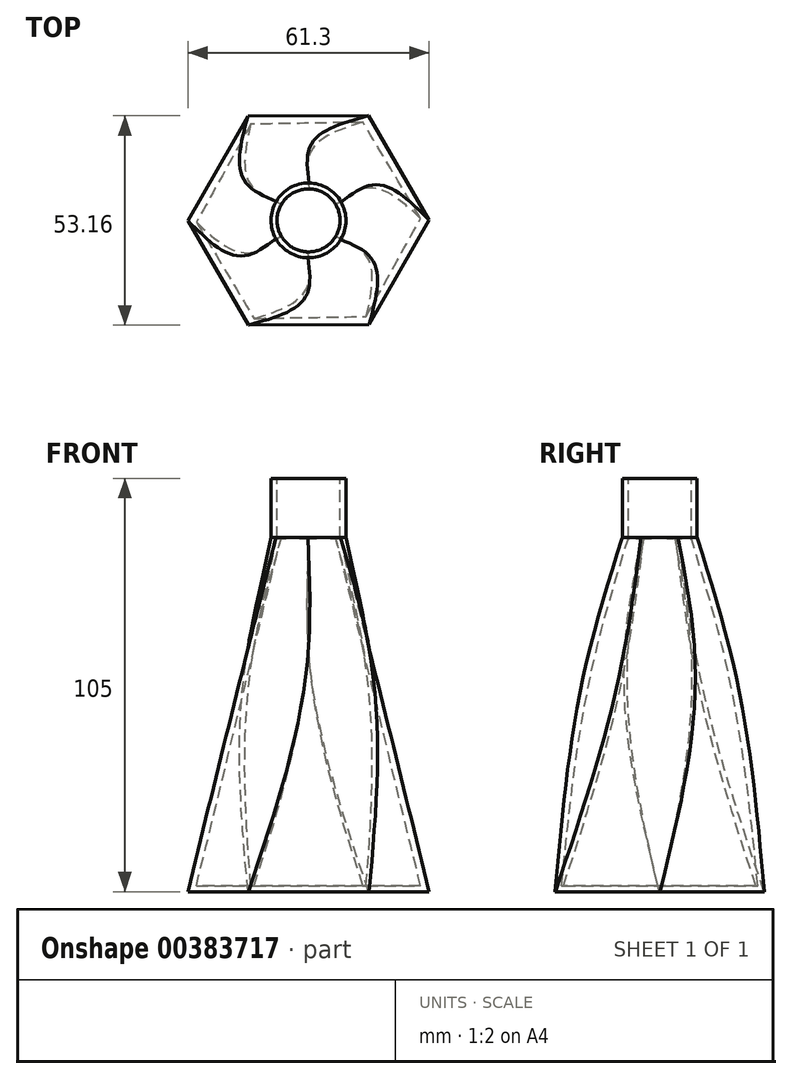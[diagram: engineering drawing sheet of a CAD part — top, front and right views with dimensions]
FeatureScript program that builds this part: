
annotation { "Feature Type Name" : "Feature", "Feature Type Description" : "" }
export const myFeature = defineFeature(function(context is Context, id is Id, definition is map)
    precondition{}
    {
        {
            var Q0;
            Q0=qCreatedBy(makeId("Top.planeOp"),FACE);
            var sketch = newSketch(context, id + "F0", { "sketchPlane" : qUnion([Q0])});
            skCircle(sketch, "E0.cCircle", {"center": v(0, 0) * mm, "radius": 26.54 * mm, "construction": true});
            skLineSegment(sketch, "E0.0", {"start": v(-30.65, -0.07) * mm, "end": v(-15.38, 26.5) * mm});
            skLineSegment(sketch, "E0.1", {"start": v(-15.38, 26.5) * mm, "end": v(15.26, 26.58) * mm});
            skLineSegment(sketch, "E0.2", {"start": v(15.26, 26.58) * mm, "end": v(30.65, 0.07) * mm});
            skLineSegment(sketch, "E0.3", {"start": v(30.65, 0.07) * mm, "end": v(15.38, -26.5) * mm});
            skLineSegment(sketch, "E0.4", {"start": v(15.38, -26.5) * mm, "end": v(-15.26, -26.58) * mm});
            skLineSegment(sketch, "E0.5", {"start": v(-15.26, -26.58) * mm, "end": v(-30.65, -0.07) * mm});
            skPoint(sketch, "E0.0.midPoint", {"position": v(-23.01, 13.22) * mm});
            skSolve(sketch);
        }
        {
            var Q0;
            Q0=qCreatedBy(makeId("Top.planeOp"),FACE);
            cPlane(context, id + "F1", {"entities" : qUnion([Q0]), "cplaneType" : CPlaneType.OFFSET, "offset" : 60 * mm, "width" : 150 * mm, "height" : 150 * mm});
        }
        {
            var Q0;
            Q0=qCreatedBy(id+"F1.planeOp",FACE);
            var sketch = newSketch(context, id + "F2", { "sketchPlane" : qUnion([Q0])});
            skCircle(sketch, "E1.cCircle", {"center": v(0, 0) * mm, "radius": 15.75 * mm, "construction": true});
            skLineSegment(sketch, "E1.0", {"start": v(-15.66, 9.24) * mm, "end": v(0.17, 18.19) * mm});
            skLineSegment(sketch, "E1.1", {"start": v(0.17, 18.19) * mm, "end": v(15.84, 8.94) * mm});
            skLineSegment(sketch, "E1.2", {"start": v(15.84, 8.94) * mm, "end": v(15.66, -9.24) * mm});
            skLineSegment(sketch, "E1.3", {"start": v(15.66, -9.24) * mm, "end": v(-0.17, -18.19) * mm});
            skLineSegment(sketch, "E1.4", {"start": v(-0.17, -18.19) * mm, "end": v(-15.84, -8.94) * mm});
            skLineSegment(sketch, "E1.5", {"start": v(-15.84, -8.94) * mm, "end": v(-15.66, 9.24) * mm});
            skPoint(sketch, "E1.0.midPoint", {"position": v(-7.74, 13.71) * mm});
            skSolve(sketch);
        }
        {
            var Q0;
            Q0=qCreatedBy(id+"F1.planeOp",FACE);
            cPlane(context, id + "F3", {"entities" : qUnion([Q0]), "cplaneType" : CPlaneType.OFFSET, "offset" : 30 * mm, "width" : 150 * mm, "height" : 150 * mm});
        }
        {
            var Q0;
            Q0=qCreatedBy(id+"F3.planeOp",FACE);
            var sketch = newSketch(context, id + "F4", { "sketchPlane" : qUnion([Q0])});
            skCircle(sketch, "E2", {"center": v(0, 0) * mm, "radius": 9.5 * mm});
            skSolve(sketch);
        }
        {
            var Q0;
            Q0=makeQuery(id+"F0.imprint","IMPRINT",FACE,{"disambiguationData":[TD([[makeQuery(id+"F0.imprint","IMPRINT",EDGE,{"derivedFrom":sQuery(id+"F0.wireOp",EDGE,"E0.0")}),-1.0]])]});
            var Q1;
            Q1=makeQuery(id+"F2.imprint","IMPRINT",FACE,{"disambiguationData":[TD([[makeQuery(id+"F2.imprint","IMPRINT",EDGE,{"derivedFrom":sQuery(id+"F2.wireOp",EDGE,"E1.0")}),-1.0]])]});
            var Q2;
            Q2=makeQuery(id+"F4.imprint","IMPRINT",FACE,{"disambiguationData":[TD([[makeQuery(id+"F4.imprint","IMPRINT",EDGE,{"derivedFrom":sQuery(id+"F4.wireOp",EDGE,"E2")}),1.0]])]});
            loft(context, id + "F5", {"sheetProfilesArray" : [{ "sheetProfileEntities" : qUnion([Q0]) }, { "sheetProfileEntities" : qUnion([Q1]) }, { "sheetProfileEntities" : qUnion([Q2]) }]});
        }
        {
            var Q0;
            Q0=makeQuery(id+"F5.opLoft","CAP_FACE",FACE,{"disambiguationData":[OSD([makeQuery(id+"F4.imprint","IMPRINT",FACE,{"disambiguationData":[TD([[makeQuery(id+"F4.imprint","IMPRINT",EDGE,{"derivedFrom":sQuery(id+"F4.wireOp",EDGE,"E2")}),1.0]])]})])],"isStart":true});
            extrude(context, id + "F6", {"entities" : qUnion([Q0]), "operationType" : NewBodyOperationType.ADD, "depth" : 15 * mm});
        }
        {
            var Q0;
            Q0=makeQuery(id+"F6.opExtrude","CAP_FACE",FACE,{"disambiguationData":[OSD([makeQuery(id+"F4.imprint","IMPRINT",FACE,{"disambiguationData":[TD([[makeQuery(id+"F4.imprint","IMPRINT",EDGE,{"derivedFrom":sQuery(id+"F4.wireOp",EDGE,"E2")}),1.0]])]})])],"isStart":false});
            shell(context, id + "F7", {"entities" : qUnion([Q0]), "thickness" : 1.5 * mm});
        }
    });
